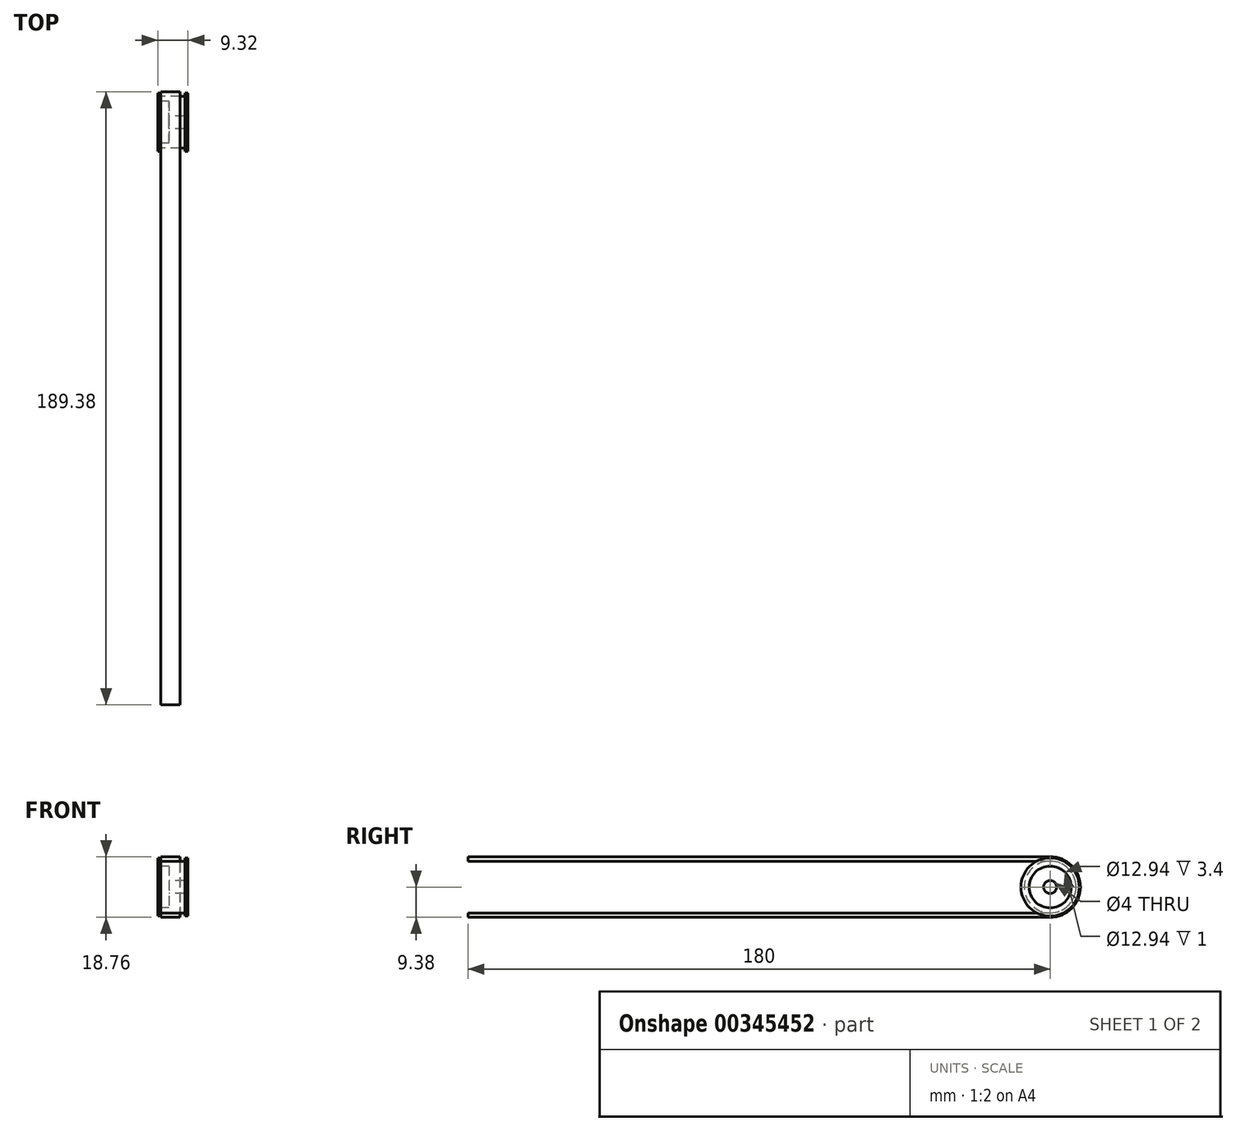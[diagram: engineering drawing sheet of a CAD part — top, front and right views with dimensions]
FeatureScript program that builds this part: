
annotation { "Feature Type Name" : "Feature", "Feature Type Description" : "" }
export const myFeature = defineFeature(function(context is Context, id is Id, definition is map)
    precondition{}
    {
        {
            var Q0;
            Q0=qCreatedBy(makeId("Front.planeOp"),FACE);
            var sketch = newSketch(context, id + "F0", { "sketchPlane" : qUnion([Q0])});
            skLineSegment(sketch, "E0", {"start": v(0, 0) * mm, "end": v(9.32, 0) * mm, "construction": true});
            skLineSegment(sketch, "E1", {"start": v(0, 6.47) * mm, "end": v(0, 9) * mm});
            skLineSegment(sketch, "E2", {"start": v(0, 9) * mm, "end": v(0.91, 9) * mm});
            skLineSegment(sketch, "E3", {"start": v(0.91, 9) * mm, "end": v(0.91, 8) * mm});
            skLineSegment(sketch, "E4", {"start": v(0.91, 8) * mm, "end": v(8.4, 8) * mm});
            skLineSegment(sketch, "E5", {"start": v(8.4, 8) * mm, "end": v(8.4, 9) * mm});
            skLineSegment(sketch, "E6", {"start": v(8.4, 9) * mm, "end": v(9.32, 9) * mm});
            skLineSegment(sketch, "E7", {"start": v(9.32, 9) * mm, "end": v(9.32, 6.47) * mm});
            skLineSegment(sketch, "E8", {"start": v(9.32, 6.47) * mm, "end": v(8.32, 6.47) * mm});
            skLineSegment(sketch, "E9", {"start": v(8.32, 6.47) * mm, "end": v(8.32, 2) * mm});
            skLineSegment(sketch, "E10", {"start": v(3.4, 6.47) * mm, "end": v(0, 6.47) * mm});
            skPoint(sketch, "E11", {"position": v(4.66, 0) * mm});
            skPoint(sketch, "E12", {"position": v(4.66, 2) * mm});
            skPoint(sketch, "E13", {"position": v(4.66, 8) * mm});
            skLineSegment(sketch, "E14", {"start": v(3.4, 6.47) * mm, "end": v(3.4, 2) * mm});
            skLineSegment(sketch, "E15", {"start": v(3.4, 2) * mm, "end": v(8.32, 2) * mm});
            skSolve(sketch);
        }
        {
            var Q0;
            Q0 = qSketchRegion(id + "F0", true);
            var Q1;
            Q1=sQuery(id+"F0.wireOp",EDGE,"E0");
            revolve(context, id + "F1", {"entities" : qUnion([Q0]), "axis" : qUnion([Q1]), "revolveType" : RevolveType.FULL});
        }
        {
            var Q0;
            Q0=makeQuery(id+"F1.opRevolve","SWEPT_FACE",FACE,{"disambiguationData":[OSD([sQuery(id+"F0.wireOp",EDGE,"E3")])]});
            var sketch = newSketch(context, id + "F2", { "sketchPlane" : qUnion([Q0])});
            skCircle(sketch, "E16.0", {"center": v(0, 0) * mm, "radius": 8 * mm, "construction": true});
            skLineSegment(sketch, "E17", {"start": v(0, -8) * mm, "end": v(-180, -8) * mm});
            skLineSegment(sketch, "E18", {"start": v(-180, -8) * mm, "end": v(-180, -9.38) * mm});
            skArc(sketch, "E19", {"start": v(0, -8) * mm, "mid": v(8, 0) * mm, "end": v(0, 8) * mm});
            skLineSegment(sketch, "E20", {"start": v(-180, -9.38) * mm, "end": v(0, -9.38) * mm});
            skArc(sketch, "E21", {"start": v(0, -9.38) * mm, "mid": v(9.38, 0) * mm, "end": v(0, 9.38) * mm});
            skLineSegment(sketch, "E22", {"start": v(0, 8) * mm, "end": v(-180, 8) * mm});
            skLineSegment(sketch, "E23", {"start": v(-180, 8) * mm, "end": v(-180, 9.38) * mm});
            skLineSegment(sketch, "E24", {"start": v(-180, 9.38) * mm, "end": v(0, 9.38) * mm});
            skSolve(sketch);
        }
        {
            var Q0;
            Q0 = qSketchRegion(id + "F2", true);
            extrude(context, id + "F3", {"entities" : qUnion([Q0]), "depth" : 6 * mm});
        }
    });
